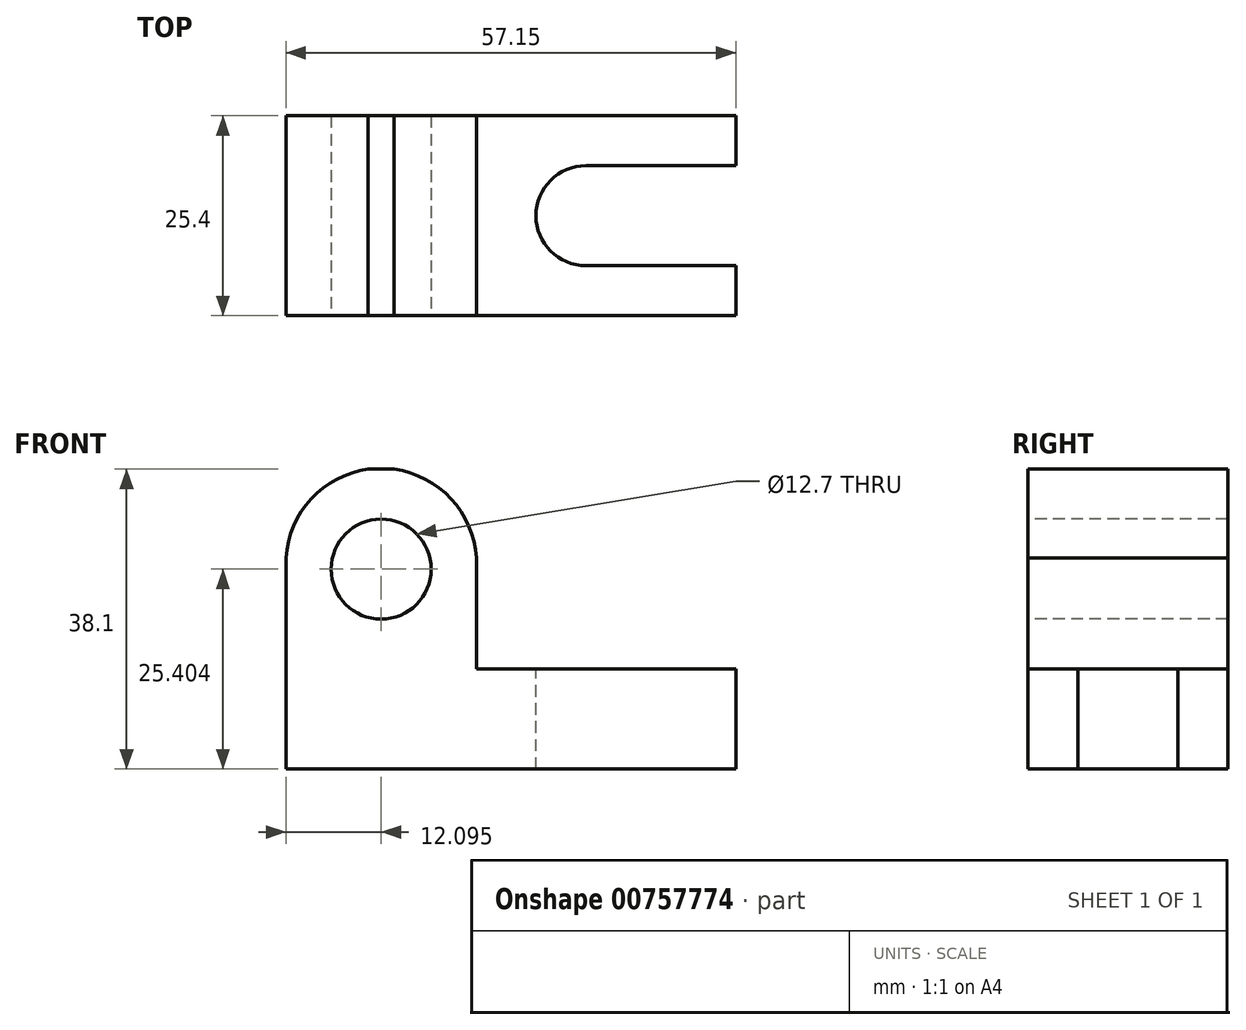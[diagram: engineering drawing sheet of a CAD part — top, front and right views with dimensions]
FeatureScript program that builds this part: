
annotation { "Feature Type Name" : "Feature", "Feature Type Description" : "" }
export const myFeature = defineFeature(function(context is Context, id is Id, definition is map)
    precondition{}
    {
        {
            var Q0;
            Q0=qCreatedBy(makeId("Front.planeOp"),FACE);
            var sketch = newSketch(context, id + "F0", { "sketchPlane" : qUnion([Q0])});
            skLineSegment(sketch, "E0", {"start": v(-30.4, 24.03) * mm, "end": v(-30.4, -14.07) * mm});
            skLineSegment(sketch, "E1", {"start": v(-30.4, -14.07) * mm, "end": v(39.44, -14.07) * mm});
            skLineSegment(sketch, "E2", {"start": v(39.44, -14.07) * mm, "end": v(39.44, -1.37) * mm});
            skLineSegment(sketch, "E3", {"start": v(39.44, -1.37) * mm, "end": v(-6.22, -1.37) * mm});
            skLineSegment(sketch, "E4", {"start": v(-6.22, -1.37) * mm, "end": v(-6.22, 24.03) * mm});
            skLineSegment(sketch, "E5", {"start": v(-6.22, 24.03) * mm, "end": v(-30.4, 24.03) * mm});
            skSolve(sketch);
        }
        {
            var Q0;
            Q0 = qSketchRegion(id + "F0", true);
            extrude(context, id + "F1", {"entities" : qUnion([Q0]), "depth" : 25.4 * mm, "offsetDistance" : 25.4 * mm});
        }
        {
            var Q0;
            Q0=makeQuery(id+"F1.opExtrude","CAP_FACE",FACE,{"disambiguationData":[OSD([sQuery(id+"F0.wireOp",EDGE,"E0"),sQuery(id+"F0.wireOp",EDGE,"E1"),sQuery(id+"F0.wireOp",EDGE,"E2"),sQuery(id+"F0.wireOp",EDGE,"E3"),sQuery(id+"F0.wireOp",EDGE,"E4"),sQuery(id+"F0.wireOp",EDGE,"E5")])],"isStart":false});
            var sketch = newSketch(context, id + "F2", { "sketchPlane" : qUnion([Q0])});
            skLineSegment(sketch, "E6", {"start": v(-30.4, 11.33) * mm, "end": v(-6.22, 11.33) * mm});
            skCircle(sketch, "E7", {"center": v(-18.31, 11.33) * mm, "radius": 6.35 * mm});
            skArc(sketch, "E8", {"start": v(-6.22, 11.33) * mm, "mid": v(-18.31, 24.15) * mm, "end": v(-30.4, 11.33) * mm});
            skSolve(sketch);
        }
        {
            var Q0;
            {var subQ0=sQuery(id+"F2.wireOp",EDGE,"E8");var subQ1=makeQuery(id+"F1.opExtrude","CAP_EDGE",EDGE,{"disambiguationData":[OSD([sQuery(id+"F0.wireOp",EDGE,"E4")])],"isStart":false});var subQ3=makeQuery(id+"F2.imprint","INTERSECT",VERTEX,{"derivedFrom":[subQ1,subQ0]});Q0=makeQuery(id+"F2.imprint","IMPRINT",FACE,{"disambiguationData":[TD([[makeQuery(id+"F2.imprint","IMPRINT",EDGE,{"disambiguationData":[TD([[subQ3,1.0]])],"derivedFrom":subQ0}),1.0]])]});}
            var Q1;
            {var subQ0=sQuery(id+"F2.wireOp",EDGE,"E8");var subQ1=makeQuery(id+"F1.opExtrude","CAP_EDGE",EDGE,{"disambiguationData":[OSD([sQuery(id+"F0.wireOp",EDGE,"E5")])],"isStart":false});var subQ2=makeQuery(id+"F2.imprint","INTERSECT",VERTEX,{"disambiguationData":[OD(0.0)],"derivedFrom":[subQ1,subQ0]});Q1=makeQuery(id+"F2.imprint","IMPRINT",FACE,{"disambiguationData":[TD([[makeQuery(id+"F2.imprint","IMPRINT",EDGE,{"disambiguationData":[TD([[subQ2,-1.0]])],"derivedFrom":subQ0}),1.0]])]});}
            var Q2;
            {var subQ0=sQuery(id+"F2.wireOp",EDGE,"E8");var subQ1=makeQuery(id+"F1.opExtrude","CAP_EDGE",EDGE,{"disambiguationData":[OSD([sQuery(id+"F0.wireOp",EDGE,"E0")])],"isStart":false});var subQ3=makeQuery(id+"F2.imprint","INTERSECT",VERTEX,{"derivedFrom":[subQ1,subQ0]});Q2=makeQuery(id+"F2.imprint","IMPRINT",FACE,{"disambiguationData":[TD([[makeQuery(id+"F2.imprint","IMPRINT",EDGE,{"disambiguationData":[TD([[subQ3,-1.0]])],"derivedFrom":subQ0}),1.0]])]});}
            var Q3;
            {var subQ0=sQuery(id+"F2.wireOp",EDGE,"E8");var subQ1=makeQuery(id+"F1.opExtrude","CAP_EDGE",EDGE,{"disambiguationData":[OSD([sQuery(id+"F0.wireOp",EDGE,"E4")])],"isStart":false});var subQ2=makeQuery(id+"F2.imprint","INTERSECT",VERTEX,{"derivedFrom":[subQ1,subQ0]});Q3=makeQuery(id+"F2.imprint","IMPRINT",FACE,{"disambiguationData":[TD([[makeQuery(id+"F2.imprint","IMPRINT",EDGE,{"disambiguationData":[TD([[subQ2,-1.0]])],"derivedFrom":subQ0}),-1.0]])]});}
            var Q4;
            {var subQ0=sQuery(id+"F2.wireOp",EDGE,"E7");var subQ1=sQuery(id+"F2.wireOp",EDGE,"E6");var subQ2=makeQuery(id+"F2.imprint","INTERSECT",VERTEX,{"disambiguationData":[OD(0.0)],"derivedFrom":[subQ1,subQ0]});Q4=makeQuery(id+"F2.imprint","IMPRINT",FACE,{"disambiguationData":[TD([[makeQuery(id+"F2.imprint","IMPRINT",EDGE,{"disambiguationData":[TD([[subQ2,-1.0]])],"derivedFrom":subQ1}),1.0]])]});}
            var Q5;
            {var subQ0=sQuery(id+"F2.wireOp",EDGE,"E7");var subQ1=sQuery(id+"F2.wireOp",EDGE,"E6");var subQ2=makeQuery(id+"F2.imprint","INTERSECT",VERTEX,{"disambiguationData":[OD(0.0)],"derivedFrom":[subQ1,subQ0]});Q5=makeQuery(id+"F2.imprint","IMPRINT",FACE,{"disambiguationData":[TD([[makeQuery(id+"F2.imprint","IMPRINT",EDGE,{"disambiguationData":[TD([[subQ2,-1.0]])],"derivedFrom":subQ1}),-1.0]])]});}
            var Q6;
            {var subQ0=sQuery(id+"F2.wireOp",EDGE,"E8");var subQ1=makeQuery(id+"F1.opExtrude","CAP_EDGE",EDGE,{"disambiguationData":[OSD([sQuery(id+"F0.wireOp",EDGE,"E5")])],"isStart":false});var subQ2=makeQuery(id+"F2.imprint","INTERSECT",VERTEX,{"disambiguationData":[OD(1.0)],"derivedFrom":[subQ1,subQ0]});Q6=makeQuery(id+"F2.imprint","IMPRINT",FACE,{"disambiguationData":[TD([[makeQuery(id+"F2.imprint","IMPRINT",EDGE,{"disambiguationData":[TD([[subQ2,-1.0]])],"derivedFrom":subQ0}),-1.0]])]});}
            extrude(context, id + "F3", {"entities" : qUnion([Q0, Q1, Q2, Q3, Q4, Q5, Q6]), "operationType" : NewBodyOperationType.REMOVE, "endBound" : BoundingType.THROUGH_ALL, "oppositeDirection" : true, "depth" : 25.4 * mm, "offsetDistance" : 25.4 * mm});
        }
        {
            var Q0;
            Q0=makeQuery(id+"F1.opExtrude","SWEPT_FACE",FACE,{"disambiguationData":[OSD([sQuery(id+"F0.wireOp",EDGE,"E3")])]});
            var sketch = newSketch(context, id + "F4", { "sketchPlane" : qUnion([Q0])});
            skLineSegment(sketch, "E9", {"start": v(26.74, 0) * mm, "end": v(26.74, -25.4) * mm});
            skLineSegment(sketch, "E10", {"start": v(7.7, 0) * mm, "end": v(7.7, -25.4) * mm});
            skCircle(sketch, "E11", {"center": v(26.74, -12.7) * mm, "radius": 6.35 * mm});
            skCircle(sketch, "E12", {"center": v(7.7, -12.7) * mm, "radius": 6.35 * mm});
            skLineSegment(sketch, "E13", {"start": v(26.74, -6.35) * mm, "end": v(7.7, -6.35) * mm});
            skLineSegment(sketch, "E14", {"start": v(7.7, -19.05) * mm, "end": v(26.74, -19.05) * mm});
            skArc(sketch, "E15", {"start": v(26.74, -25.4) * mm, "mid": v(39.56, -12.7) * mm, "end": v(26.74, 0) * mm});
            skSolve(sketch);
        }
        {
            var Q0;
            {var subQ0=sQuery(id+"F4.wireOp",EDGE,"E12");var subQ1=sQuery(id+"F4.wireOp",EDGE,"E10");var subQ2=makeQuery(id+"F4.imprint","INTERSECT",VERTEX,{"derivedFrom":[subQ1,subQ0,sQuery(id+"F4.wireOp",EDGE,"E13")]});Q0=makeQuery(id+"F4.imprint","IMPRINT",FACE,{"disambiguationData":[TD([[makeQuery(id+"F4.imprint","IMPRINT",EDGE,{"disambiguationData":[TD([[subQ2,-1.0]])],"derivedFrom":subQ1}),-1.0]])]});}
            var Q1;
            {var subQ0=sQuery(id+"F4.wireOp",EDGE,"E12");var subQ1=sQuery(id+"F4.wireOp",EDGE,"E10");var subQ2=makeQuery(id+"F4.imprint","INTERSECT",VERTEX,{"derivedFrom":[subQ1,subQ0,sQuery(id+"F4.wireOp",EDGE,"E13")]});Q1=makeQuery(id+"F4.imprint","IMPRINT",FACE,{"disambiguationData":[TD([[makeQuery(id+"F4.imprint","IMPRINT",EDGE,{"disambiguationData":[TD([[subQ2,-1.0]])],"derivedFrom":subQ1}),1.0]])]});}
            var Q2;
            {var subQ0=sQuery(id+"F4.wireOp",EDGE,"E13");Q2=makeQuery(id+"F4.imprint","IMPRINT",FACE,{"disambiguationData":[TD([[makeQuery(id+"F4.imprint","IMPRINT",EDGE,{"derivedFrom":subQ0}),1.0]])]});}
            var Q3;
            {var subQ0=sQuery(id+"F4.wireOp",EDGE,"E15");var subQ1=makeQuery(id+"F1.opExtrude","CAP_EDGE",EDGE,{"disambiguationData":[OSD([sQuery(id+"F0.wireOp",EDGE,"E3")])],"isStart":false});var subQ3=makeQuery(id+"F4.imprint","INTERSECT",VERTEX,{"derivedFrom":[subQ1,subQ0]});Q3=makeQuery(id+"F4.imprint","IMPRINT",FACE,{"disambiguationData":[TD([[makeQuery(id+"F4.imprint","IMPRINT",EDGE,{"disambiguationData":[TD([[subQ3,1.0]])],"derivedFrom":subQ0}),1.0]])]});}
            var Q4;
            {var subQ0=sQuery(id+"F4.wireOp",EDGE,"E15");var subQ1=makeQuery(id+"F1.opExtrude","SWEPT_EDGE",EDGE,{"disambiguationData":[OSD([sQuery(id+"F0.wireOp",EDGE,"E2"),sQuery(id+"F0.wireOp",EDGE,"E3")])]});var subQ2=makeQuery(id+"F4.imprint","INTERSECT",VERTEX,{"disambiguationData":[OD(0.0)],"derivedFrom":[subQ1,subQ0]});Q4=makeQuery(id+"F4.imprint","IMPRINT",FACE,{"disambiguationData":[TD([[makeQuery(id+"F4.imprint","IMPRINT",EDGE,{"disambiguationData":[TD([[subQ2,-1.0]])],"derivedFrom":subQ0}),1.0]])]});}
            var Q5;
            {var subQ0=sQuery(id+"F4.wireOp",EDGE,"E15");var subQ1=makeQuery(id+"F1.opExtrude","CAP_EDGE",EDGE,{"disambiguationData":[OSD([sQuery(id+"F0.wireOp",EDGE,"E3")])],"isStart":true});var subQ3=makeQuery(id+"F4.imprint","INTERSECT",VERTEX,{"derivedFrom":[subQ1,subQ0]});Q5=makeQuery(id+"F4.imprint","IMPRINT",FACE,{"disambiguationData":[TD([[makeQuery(id+"F4.imprint","IMPRINT",EDGE,{"disambiguationData":[TD([[subQ3,-1.0]])],"derivedFrom":subQ0}),1.0]])]});}
            var Q6;
            {var subQ0=sQuery(id+"F4.wireOp",EDGE,"E11");var subQ1=sQuery(id+"F4.wireOp",EDGE,"E9");var subQ2=makeQuery(id+"F4.imprint","INTERSECT",VERTEX,{"derivedFrom":[subQ1,subQ0,sQuery(id+"F4.wireOp",EDGE,"E13")]});Q6=makeQuery(id+"F4.imprint","IMPRINT",FACE,{"disambiguationData":[TD([[makeQuery(id+"F4.imprint","IMPRINT",EDGE,{"disambiguationData":[TD([[subQ2,-1.0]])],"derivedFrom":subQ1}),-1.0]])]});}
            var Q7;
            {var subQ0=sQuery(id+"F4.wireOp",EDGE,"E11");var subQ1=sQuery(id+"F4.wireOp",EDGE,"E9");var subQ2=makeQuery(id+"F4.imprint","INTERSECT",VERTEX,{"derivedFrom":[subQ1,subQ0,sQuery(id+"F4.wireOp",EDGE,"E13")]});Q7=makeQuery(id+"F4.imprint","IMPRINT",FACE,{"disambiguationData":[TD([[makeQuery(id+"F4.imprint","IMPRINT",EDGE,{"disambiguationData":[TD([[subQ2,-1.0]])],"derivedFrom":subQ1}),1.0]])]});}
            var Q8;
            {var subQ0=sQuery(id+"F4.wireOp",EDGE,"E15");var subQ1=sQuery(id+"F0.wireOp",EDGE,"E3");var subQ2=makeQuery(id+"F1.opExtrude","CAP_EDGE",EDGE,{"disambiguationData":[OSD([subQ1])],"isStart":false});var subQ3=makeQuery(id+"F4.imprint","INTERSECT",VERTEX,{"derivedFrom":[subQ2,subQ0]});Q8=makeQuery(id+"F4.imprint","IMPRINT",FACE,{"disambiguationData":[TD([[makeQuery(id+"F4.imprint","IMPRINT",EDGE,{"disambiguationData":[TD([[subQ3,-1.0]])],"derivedFrom":subQ0}),-1.0]])]});}
            var Q9;
            {var subQ0=sQuery(id+"F4.wireOp",EDGE,"E15");var subQ1=sQuery(id+"F0.wireOp",EDGE,"E3");var subQ4=makeQuery(id+"F1.opExtrude","CAP_EDGE",EDGE,{"disambiguationData":[OSD([subQ1])],"isStart":true});var subQ5=makeQuery(id+"F4.imprint","INTERSECT",VERTEX,{"derivedFrom":[subQ4,subQ0]});Q9=makeQuery(id+"F4.imprint","IMPRINT",FACE,{"disambiguationData":[TD([[makeQuery(id+"F4.imprint","IMPRINT",EDGE,{"disambiguationData":[TD([[subQ5,1.0]])],"derivedFrom":subQ0}),-1.0]])]});}
            extrude(context, id + "F5", {"entities" : qUnion([Q0, Q1, Q2, Q3, Q4, Q5, Q6, Q7, Q8, Q9]), "operationType" : NewBodyOperationType.REMOVE, "endBound" : BoundingType.THROUGH_ALL, "oppositeDirection" : true, "depth" : 25.4 * mm, "offsetDistance" : 25.4 * mm});
        }
    });
